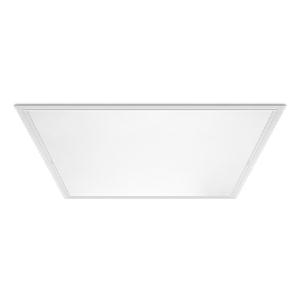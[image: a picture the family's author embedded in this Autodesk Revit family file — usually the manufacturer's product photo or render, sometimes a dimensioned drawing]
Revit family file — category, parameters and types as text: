
# Revit family: 3f_filippi_-_l_340_luce_diffusa_vs_ip65v_3f_filippi_-_23903_-_l_340_25w-840_dali_vs_ip65v_596x596
name_source: partatom
category: Lighting Fixtures
units: mm (PartAtom-declared; Revit-internal decimal feet)

## family parameters
Cut with Voids When Loaded = No
Host = Face
Light Source = No
Part Type = Normal
Room Calculation Point = No
Round Connector Dimension = Use Diameter
Shared = No

## types (1)
- 3F Filippi - L 340 Luce Diffusa VS IP65V (1 x LED, 3499 lm, 29 W, 4000 K)
    Apparent Load = 29 VA
    Approval mark = ENEC
    CIE Flux Codes = 61 89 98 100 100
    Color Rendering = 80
    Color Temperature = 4000 K
    Control Gear = Electronic transformer
    Default Elevation = 1800 mm
    Description = ILLUMINOTECHNICAL
Luminous efficiency 100% (DLOR 100%, ULOR 0%).
Initial luminous flux of the luminaire 3499 lm.
Direct symmetric distribution.
Installation Interdistance Transv.D = 1.17 x hu - Long.D = 1.14 x hu.
Average luminance <3000 cd/m² for radial angles >65°.
Tabular UGR (CIE 117 - 4H-8H; S=0.25H; 70/50/20): RUG 17.6 - 17.4.
Beam angle: 91° - 88°.
Luminous efficacy 121 lm/W.
Lifetime (L93/B10): 30000 h. (tq+25°C)
Lifetime (L90/B10): 50000 h. (tq+25°C)
Lifetime (L85/B10): 80000 h. (tq+25°C)
Lifetime (L80/B10): 100000 h. (tq+25°C)
Sudden decreased luminous flux after 50000 hours: 0% (C0).
Photobiological safety in compliance with IEC/TR 62778: RG0 risk exempt, (IEC 62471).
In compliance with IEC/EN 62722-2-1 - IEC/EN 62717 standards.

SOURCE
Squared LED module 25W/840.
Energy efficiency class (UE 2019/2020 - UE 2019/2015): C.
CIE 13.3 Colour rendering index: CRI >80 (R9 <50%).
IES TM-30 Fidelity Index: Rf = 84 Rg = 95.
CCT nominal colour temperature 4000 K.
Colour initial tolerance (MacAdam): SDCM 3.

MECHANICAL
Housing in hot-galvanised steel, painted in white polyester.
Perimetral frame in white polycarbonate.
VS moulded glass, anti-glare, tempered, non-combustible, thickness 4 mm.
Luminaire with limited surface temperature. - D - (EN 60598-2-24)
Dimensions: 596x596 mm, height 80 mm. Weight 6.4 kg.
IP65 protection degree for exposed part, IP40 for recessed part.
Mechanical strength to impacts IK08 (5 joule).
Glow-wire test resistance 960°C.

ELECTRICAL
Wiring on a separate unit.
Halogen Free DALI-2 DATI (Parts 251, 252, 253), PUSH-DIM, electronic wiring 230V-50/60Hz, power factor 0.95 at full load, THD <25%, constant output current, SELV, class II, 1 driver, 1 DALI addresse.
Power of the luminaire 29 W.
CE - IEC 60598-1 - EN 60598-1.
SAFE FLICKER: PstLM=<1 and SVM=<0.4 (IEC TR 61547-1 and IEC TR 63158), to ensure a more comfortable and safe light.
Luminaire compliant with EN 60598-2-22 for power supply from a centralised emergency system CPSS (Central Power Supply System), not incorporated in the luminaire - high risk areas excluded. The default power and flux are 100% in AC and 100% in DC.
Ambient temperature from 0°C to +40°C.
Temperature class T6 max 85°C.
Relative humidity UR: <85%.

INSTALLATION
Lay-on or pull-up recessed fitting using frame and anti-fall safety cable accessories.
All accessories dedicated to this product are available on the Catalog and on our website www.3F-Filippi.com.

APPLICATIONS
In environments requiring protection and simplified cleaning.
Hospitals, pharmaceutical, chemical, aseptic laboratories, sterilised rooms.
Environments: with VDTs, meeting rooms, offices.
Environments: architectural, commercial, staterooms, banks.
Environments where demanding visual tasks are performed and soft diffuse light is required for optimal visual comfort and total shielding of the light source.

LIGHT MANAGEMENT
Recommended minimum setting: 10%.
The luminaire, equipped with (DALI-2 DATI) driver, can be controlled manually with 3F Easy Dim technology or automatically/manually with wired or wireless DALI/D2D control systems.
The D2D driver guarantees interoperability with other devices with the same certification by making the following information available:
Device Data (Part 251), Energy Report (Part 252), Diagnosis & Maintenance (Part 253).
In electrical systems without a regulation system (manual or automatic) and DALI bus, a suitable jumper must be made on the DA-DA terminals of the appliance.

WARNING
Luminaire designed for disposal/recycling at end-of-life.
Replaceable (LED only) light source by a professional. Replaceable control gear by a professional.
    Height = 0 mm  [stored 0 ft]
    Lamp = 1 x LED
    Lamp Light Flux = 3499 lm
    Lamp Power = 29 W
    Lamp count = 1
    Length = 596 mm
    Lifetime = 50000 h
    Luminous efficacy = 121 lm/W
    Manufacturer = 3F Filippi
    ModVariant = No
    Model = 3F Filippi - 23903 - L 340 25W-840 DALI VS IP65V 596x596
    Mounting Place = Ceiling
    Mounting Type = Recessed
    Number of Poles = 1
    OnlyDefault = Yes
    Power Factor = 1
    Product Name = 3F Filippi - L 340 Luce Diffusa VS IP65V
    Product group = recessed luminaire
    ProductGroupID = 4
    Protection Class = Protection class II
    Protection Degree = IP 40
    RLX_Detail_Level = 1
    RLX_Emergency_Light_Flux = 0 lm
    RLX_Emergency_Type = 0
    RLX_Emergency_Type_DB = No
    RlxData = <blob elided: 155617 chars, md5=f76e94c8>
    Socket = socket
    Standby Power = 0 W
    System Light Flux = 3499 lm
    System Power = 29 W
    Type Comments = Product without accessories
    Type Image = 3ffilippi_l_340_luce_diffusa_vs.jpg
    URL = http://relux.com
    VarID = ---
    Voltage = 0 V
    Weight = 0.00 kg
    Width = 596 mm

note: [stored X ft] marks values corroborated as IEEE doubles in the binary element streams (Revit-internal decimal feet)

## geometry (parser evidence)
native form markers: Blend x4, Sweep x8
no freeform markers — native parametric forms only
